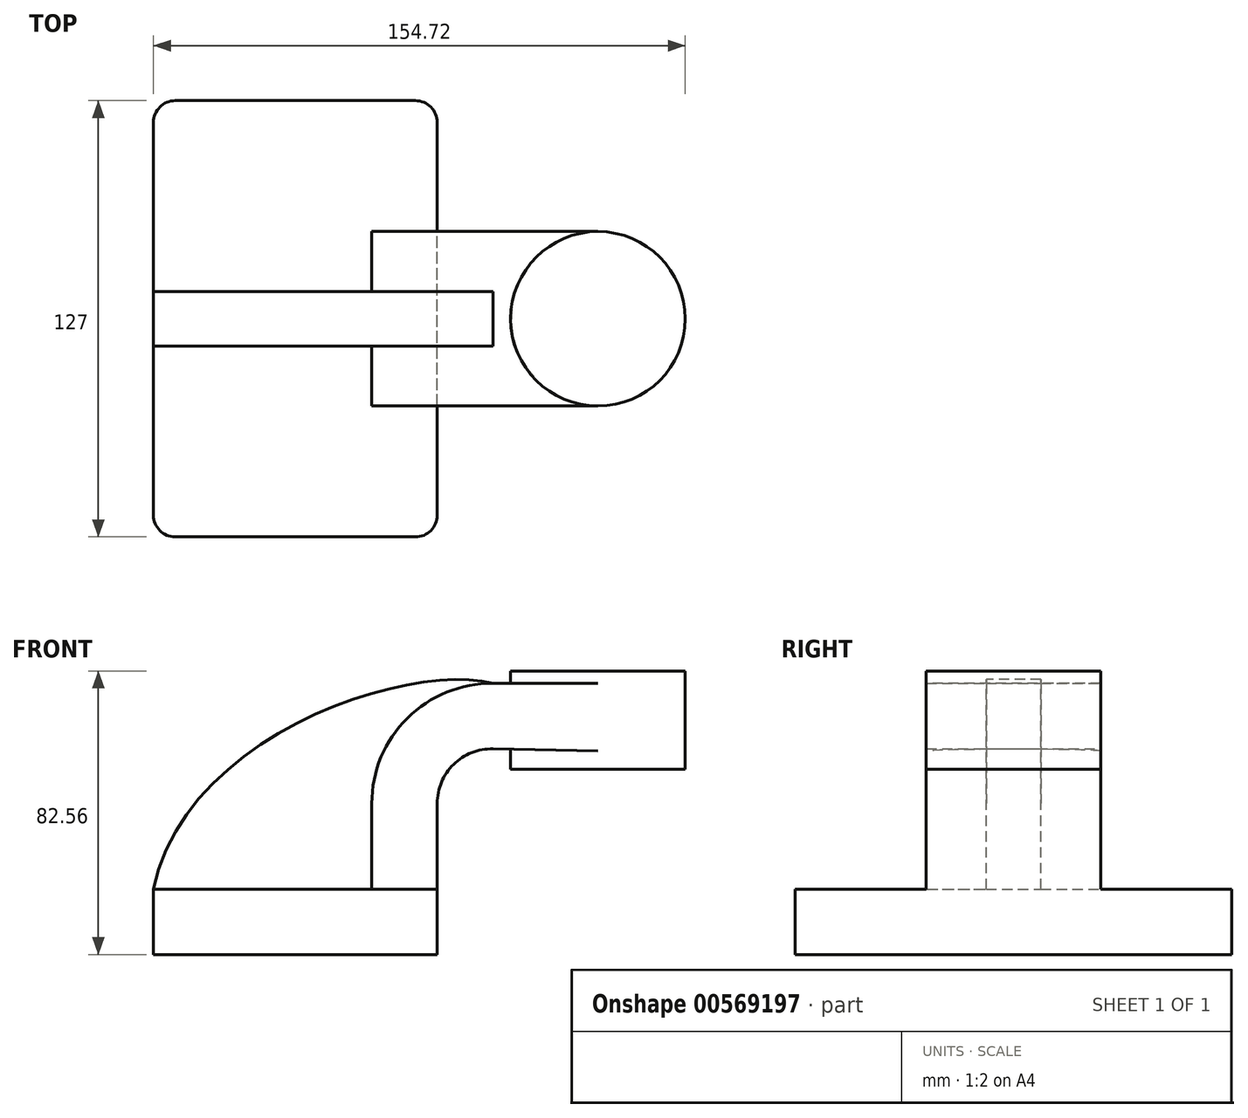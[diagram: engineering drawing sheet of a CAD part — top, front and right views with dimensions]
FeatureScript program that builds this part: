
annotation { "Feature Type Name" : "Feature", "Feature Type Description" : "" }
export const myFeature = defineFeature(function(context is Context, id is Id, definition is map)
    precondition{}
    {
        {
            var Q0;
            Q0=qCreatedBy(makeId("Front.planeOp"),FACE);
            var sketch = newSketch(context, id + "F0", { "sketchPlane" : qUnion([Q0])});
            skLineSegment(sketch, "E0.bottom", {"start": v(-41.28, 9.52) * mm, "end": v(41.28, 9.53) * mm});
            skLineSegment(sketch, "E0.top", {"start": v(-41.28, -9.53) * mm, "end": v(41.28, -9.53) * mm});
            skLineSegment(sketch, "E0.left", {"start": v(-41.28, 9.52) * mm, "end": v(-41.27, -9.53) * mm});
            skLineSegment(sketch, "E0.right", {"start": v(41.28, 9.53) * mm, "end": v(41.28, -9.52) * mm});
            skPoint(sketch, "E0.middle", {"position": v(0, 0) * mm});
            skLineSegment(sketch, "E1.bottom", {"start": v(113.44, 44.45) * mm, "end": v(62.64, 44.45) * mm});
            skLineSegment(sketch, "E1.top", {"start": v(113.44, 73.03) * mm, "end": v(62.64, 73.03) * mm});
            skLineSegment(sketch, "E1.left", {"start": v(113.44, 44.45) * mm, "end": v(113.44, 73.03) * mm});
            skLineSegment(sketch, "E1.right", {"start": v(62.64, 44.45) * mm, "end": v(62.64, 73.03) * mm});
            skPoint(sketch, "E1.middle", {"position": v(88.04, 58.74) * mm});
            skLineSegment(sketch, "E2", {"start": v(41.27, 9.53) * mm, "end": v(41.27, 34.45) * mm});
            skArc(sketch, "E3", {"start": v(41.28, 34.45) * mm, "mid": v(46.05, 45.8) * mm, "end": v(57.5, 50.33) * mm});
            skArc(sketch, "E4.0", {"start": v(22.23, 34.45) * mm, "mid": v(32.57, 59.27) * mm, "end": v(57.5, 69.38) * mm});
            skLineSegment(sketch, "E4.1", {"start": v(22.22, 9.53) * mm, "end": v(22.22, 34.45) * mm});
            skLineSegment(sketch, "E5", {"start": v(57.5, 69.38) * mm, "end": v(57.5, 50.33) * mm});
            skFitSpline(sketch, "E6", {"points": [v(-41.28, 9.52) * mm, v(57.5, 69.38) * mm], "startDerivative": vector(28.67, 137.95) * mm, "endDerivative": vector(69.24, -19) * mm});
            skLineSegment(sketch, "E7", {"start": v(88.04, 73.03) * mm, "end": v(88.04, 44.45) * mm});
            skLineSegment(sketch, "E8", {"start": v(57.5, 69.38) * mm, "end": v(88.04, 69.38) * mm});
            skLineSegment(sketch, "E9", {"start": v(57.5, 50.33) * mm, "end": v(88.04, 49.67) * mm});
            skSolve(sketch);
        }
        {
            var Q0;
            Q0=makeQuery(id+"F0.imprint","IMPRINT",FACE,{"disambiguationData":[TD([[makeQuery(id+"F0.imprint","IMPRINT",EDGE,{"derivedFrom":sQuery(id+"F0.wireOp",EDGE,"E0.top")}),1.0]])]});
            extrude(context, id + "F1", {"entities" : qUnion([Q0]), "endBound" : BoundingType.SYMMETRIC, "depth" : 127 * mm, "offsetDistance" : 25.4 * mm});
        }
        {
            var Q0;
            {var subQ1=sQuery(id+"F0.wireOp",EDGE,"E2");Q0=makeQuery(id+"F0.imprint","IMPRINT",FACE,{"disambiguationData":[TD([[makeQuery(id+"F0.imprint","IMPRINT",EDGE,{"derivedFrom":subQ1}),1.0]])]});}
            var Q1;
            {var subQ5=sQuery(id+"F0.wireOp",EDGE,"E5");Q1=makeQuery(id+"F0.imprint","IMPRINT",FACE,{"disambiguationData":[TD([[makeQuery(id+"F0.imprint","IMPRINT",EDGE,{"derivedFrom":subQ5}),-1.0]])]});}
            var Q2;
            {var subQ0=sQuery(id+"F0.wireOp",EDGE,"E9");var subQ1=sQuery(id+"F0.wireOp",EDGE,"E1.right");var subQ2=makeQuery(id+"F0.imprint","INTERSECT",VERTEX,{"derivedFrom":[subQ1,subQ0]});Q2=makeQuery(id+"F0.imprint","IMPRINT",FACE,{"disambiguationData":[TD([[makeQuery(id+"F0.imprint","IMPRINT",EDGE,{"disambiguationData":[TD([[subQ2,-1.0]])],"derivedFrom":subQ1}),-1.0]])]});}
            var Q3;
            {var subQ5=sQuery(id+"F0.wireOp",EDGE,"E5");Q3=makeQuery(id+"F0.imprint","IMPRINT",FACE,{"disambiguationData":[TD([[makeQuery(id+"F0.imprint","IMPRINT",EDGE,{"derivedFrom":subQ5}),1.0]])]});}
            extrude(context, id + "F2", {"entities" : qUnion([Q0, Q1, Q2, Q3]), "operationType" : NewBodyOperationType.ADD, "endBound" : BoundingType.SYMMETRIC, "depth" : 50.8 * mm, "offsetDistance" : 25.4 * mm});
        }
        {
            var Q0;
            {var subQ0=sQuery(id+"F0.wireOp",EDGE,"E4.1");Q0=makeQuery(id+"F0.imprint","IMPRINT",FACE,{"disambiguationData":[TD([[makeQuery(id+"F0.imprint","IMPRINT",EDGE,{"derivedFrom":subQ0}),1.0]])]});}
            extrude(context, id + "F3", {"entities" : qUnion([Q0]), "operationType" : NewBodyOperationType.ADD, "endBound" : BoundingType.SYMMETRIC, "depth" : 15.88 * mm, "offsetDistance" : 25.4 * mm});
        }
        {
            var Q0;
            {var subQ4=sQuery(id+"F0.wireOp",EDGE,"E1.left");Q0=makeQuery(id+"F0.imprint","IMPRINT",FACE,{"disambiguationData":[TD([[makeQuery(id+"F0.imprint","IMPRINT",EDGE,{"derivedFrom":subQ4}),1.0]])]});}
            var Q1;
            Q1=sQuery(id+"F0.wireOp",EDGE,"E7");
            revolve(context, id + "F4", {"operationType" : NewBodyOperationType.ADD, "entities" : qUnion([Q0]), "axis" : qUnion([Q1]), "revolveType" : RevolveType.FULL});
        }
        {
            var Q0;
            Q0=makeQuery(id+"F1.opExtrude","CAP_EDGE",EDGE,{"disambiguationData":[OSD([sQuery(id+"F0.wireOp",EDGE,"E0.right")])],"isStart":false});
            var Q1;
            Q1=makeQuery(id+"F1.opExtrude","CAP_EDGE",EDGE,{"disambiguationData":[OSD([sQuery(id+"F0.wireOp",EDGE,"E0.left")])],"isStart":false});
            var Q2;
            Q2=makeQuery(id+"F1.opExtrude","CAP_EDGE",EDGE,{"disambiguationData":[OSD([sQuery(id+"F0.wireOp",EDGE,"E0.left")])],"isStart":true});
            var Q3;
            Q3=makeQuery(id+"F1.opExtrude","CAP_EDGE",EDGE,{"disambiguationData":[OSD([sQuery(id+"F0.wireOp",EDGE,"E0.right")])],"isStart":true});
            fillet(context, id + "F5", {"entities" : qUnion([Q0, Q1, Q2, Q3]), "radius" : 6.35 * mm, "tangentPropagation" : true, "allowEdgeOverflow" : false});
        }
    });
